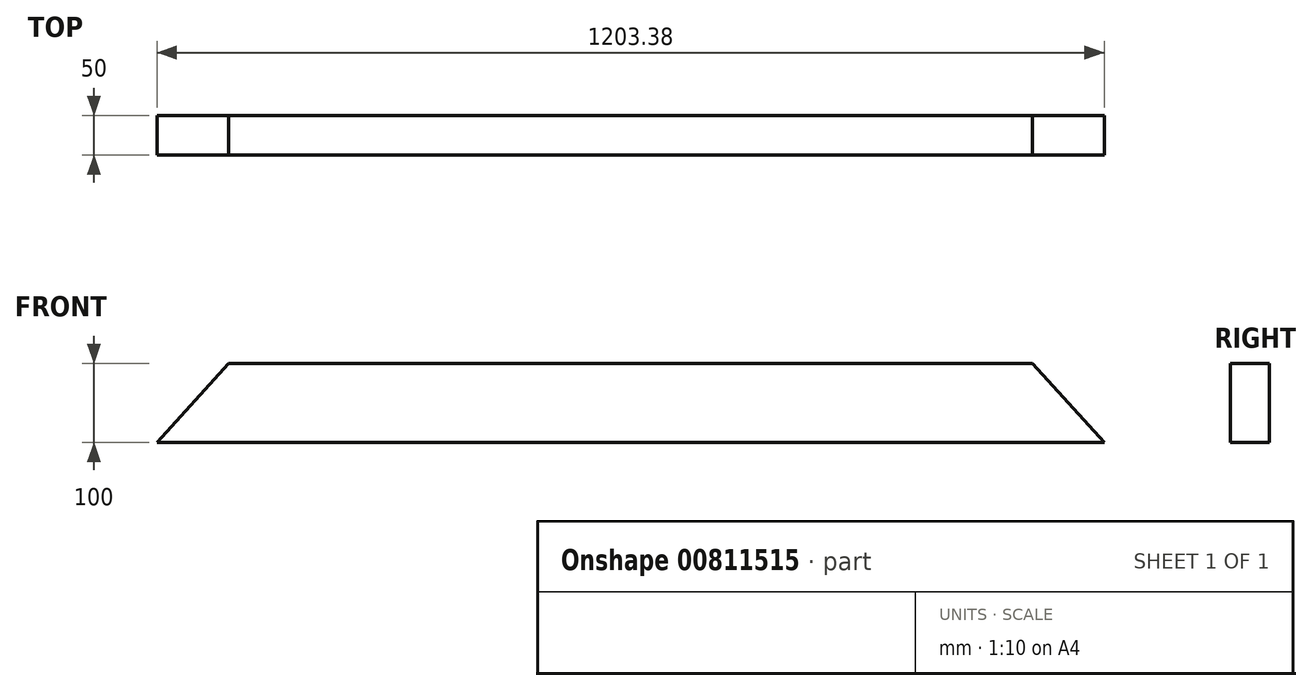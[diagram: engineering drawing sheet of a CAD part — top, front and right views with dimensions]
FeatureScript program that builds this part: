
annotation { "Feature Type Name" : "Feature", "Feature Type Description" : "" }
export const myFeature = defineFeature(function(context is Context, id is Id, definition is map)
    precondition{}
    {
        {
            var Q0;
            Q0=qCreatedBy(makeId("Front.planeOp"),FACE);
            var sketch = newSketch(context, id + "F0", { "sketchPlane" : qUnion([Q0])});
            skLineSegment(sketch, "E0", {"start": v(-1197.5, 0) * mm, "end": v(1197.5, 0) * mm, "construction": true});
            skLineSegment(sketch, "E1", {"start": v(1197.5, 0) * mm, "end": v(0, 1310) * mm, "construction": true});
            skLineSegment(sketch, "E2", {"start": v(0, 1310) * mm, "end": v(-1197.5, 0) * mm, "construction": true});
            skLineSegment(sketch, "E3", {"start": v(0, 1310) * mm, "end": v(-135.49, 1310) * mm, "construction": true});
            skLineSegment(sketch, "E4", {"start": v(-1197.5, 0) * mm, "end": v(-1332.99, 0) * mm, "construction": true});
            skLineSegment(sketch, "E5", {"start": v(-1332.99, 0) * mm, "end": v(-135.49, 1310) * mm, "construction": true});
            skLineSegment(sketch, "E6", {"start": v(-510.28, 900) * mm, "end": v(510.28, 900) * mm});
            skLineSegment(sketch, "E7", {"start": v(-510.28, 900) * mm, "end": v(-601.69, 800) * mm});
            skLineSegment(sketch, "E8", {"start": v(-601.69, 800) * mm, "end": v(601.69, 800) * mm});
            skLineSegment(sketch, "E9", {"start": v(601.69, 800) * mm, "end": v(510.28, 900) * mm});
            skPoint(sketch, "E10", {"position": v(0, 800) * mm});
            skPoint(sketch, "E11", {"position": v(0, 900) * mm});
            skSolve(sketch);
        }
        {
            var Q0;
            Q0=makeQuery(id+"F0.imprint","IMPRINT",FACE,{"disambiguationData":[TD([[makeQuery(id+"F0.imprint","IMPRINT",EDGE,{"derivedFrom":sQuery(id+"F0.wireOp",EDGE,"E6")}),-1.0]])]});
            extrude(context, id + "F1", {"entities" : qUnion([Q0]), "depth" : 50 * mm, "offsetDistance" : 25 * mm});
        }
    });
